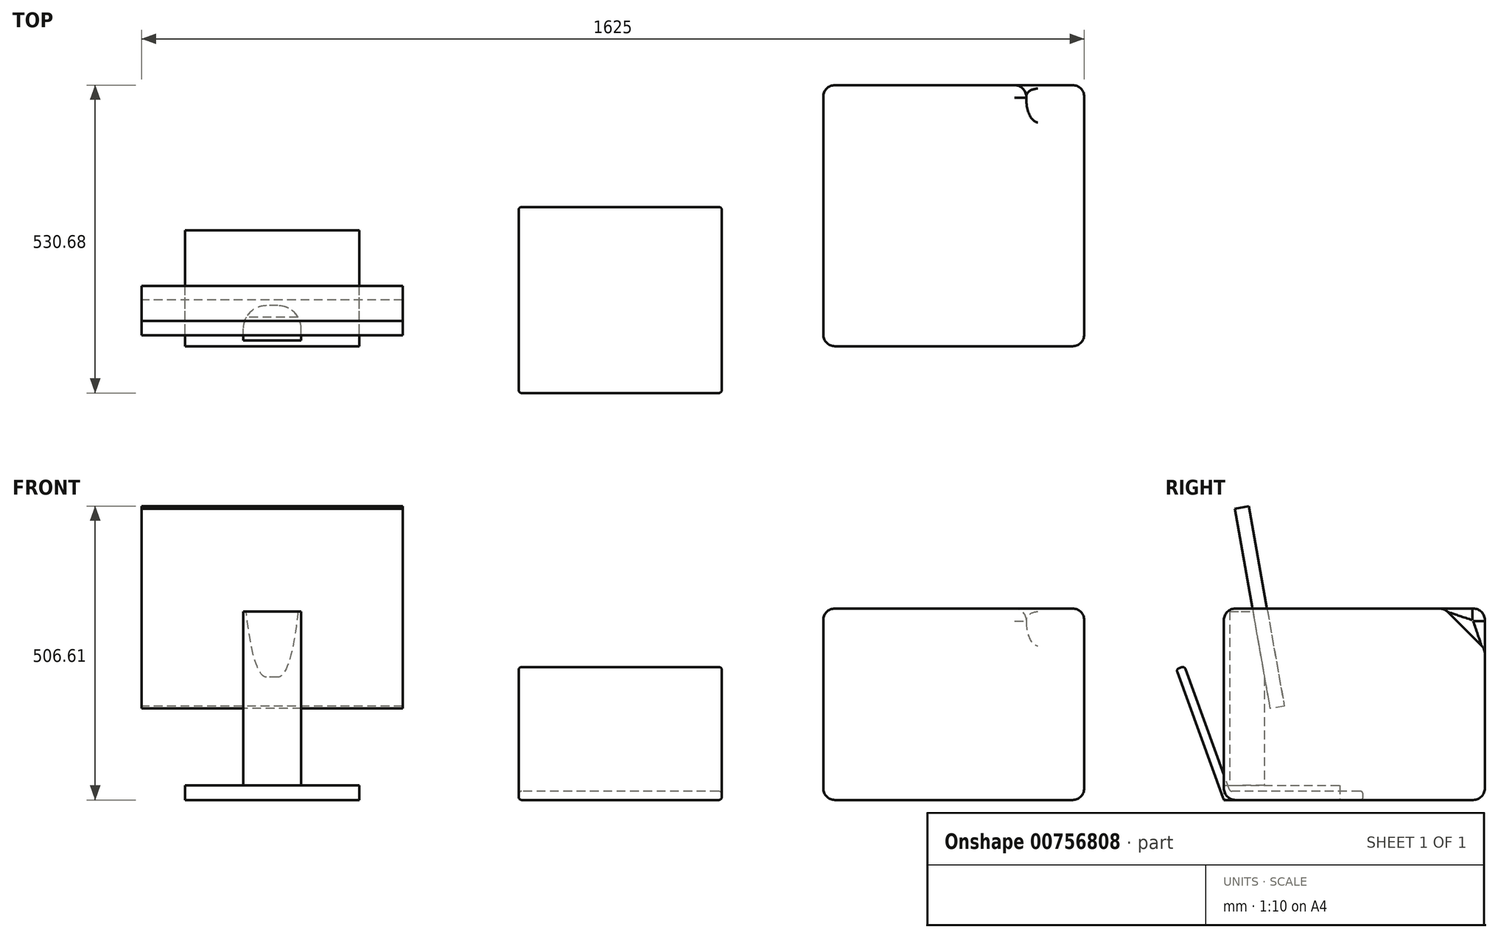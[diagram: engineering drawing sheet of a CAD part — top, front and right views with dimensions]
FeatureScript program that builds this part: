
annotation { "Feature Type Name" : "Feature", "Feature Type Description" : "" }
export const myFeature = defineFeature(function(context is Context, id is Id, definition is map)
    precondition{}
    {
        {
            var Q0;
            Q0=qCreatedBy(makeId("Right.planeOp"),FACE);
            var sketch = newSketch(context, id + "F0", { "sketchPlane" : qUnion([Q0])});
            skLineSegment(sketch, "E0", {"start": v(0, 0) * mm, "end": v(240, 0) * mm});
            skLineSegment(sketch, "E1", {"start": v(240, 0) * mm, "end": v(240, 15) * mm});
            skLineSegment(sketch, "E2", {"start": v(240, 15) * mm, "end": v(10.5, 15) * mm});
            skLineSegment(sketch, "E3", {"start": v(10.5, 15) * mm, "end": v(-67.99, 230.66) * mm});
            skLineSegment(sketch, "E4", {"start": v(-67.99, 230.66) * mm, "end": v(-82.08, 225.53) * mm});
            skLineSegment(sketch, "E5", {"start": v(-82.08, 225.53) * mm, "end": v(0, 0) * mm});
            skSolve(sketch);
        }
        {
            var Q0;
            Q0 = qSketchRegion(id + "F0", true);
            extrude(context, id + "F1", {"entities" : qUnion([Q0]), "endBound" : BoundingType.SYMMETRIC, "depth" : 350 * mm, "offsetDistance" : 25 * mm});
        }
        {
            var Q0;
            Q0=makeQuery(id+"F1.opExtrude","CAP_FACE",FACE,{"disambiguationData":[OSD([sQuery(id+"F0.wireOp",EDGE,"E0"),sQuery(id+"F0.wireOp",EDGE,"E1"),sQuery(id+"F0.wireOp",EDGE,"E2"),sQuery(id+"F0.wireOp",EDGE,"E3"),sQuery(id+"F0.wireOp",EDGE,"E4"),sQuery(id+"F0.wireOp",EDGE,"E5")])],"isStart":false});
            var Q1;
            Q1=makeQuery(id+"F1.opExtrude","SWEPT_EDGE",EDGE,{"disambiguationData":[OSD([sQuery(id+"F0.wireOp",EDGE,"E0"),sQuery(id+"F0.wireOp",EDGE,"E1")])]});
            var Q2;
            Q2=makeQuery(id+"F1.opExtrude","CAP_FACE",FACE,{"disambiguationData":[OSD([sQuery(id+"F0.wireOp",EDGE,"E0"),sQuery(id+"F0.wireOp",EDGE,"E1"),sQuery(id+"F0.wireOp",EDGE,"E2"),sQuery(id+"F0.wireOp",EDGE,"E3"),sQuery(id+"F0.wireOp",EDGE,"E4"),sQuery(id+"F0.wireOp",EDGE,"E5")])],"isStart":true});
            var Q3;
            Q3=makeQuery(id+"F1.opExtrude","SWEPT_EDGE",EDGE,{"disambiguationData":[OSD([sQuery(id+"F0.wireOp",EDGE,"E2"),sQuery(id+"F0.wireOp",EDGE,"E3")])]});
            var Q4;
            Q4=makeQuery(id+"F1.opExtrude","SWEPT_EDGE",EDGE,{"disambiguationData":[OSD([sQuery(id+"F0.wireOp",EDGE,"E1"),sQuery(id+"F0.wireOp",EDGE,"E2")])]});
            var Q5;
            Q5=makeQuery(id+"F1.opExtrude","SWEPT_FACE",FACE,{"disambiguationData":[OSD([sQuery(id+"F0.wireOp",EDGE,"E0")])]});
            var Q6;
            Q6=makeQuery(id+"F1.opExtrude","SWEPT_FACE",FACE,{"disambiguationData":[OSD([sQuery(id+"F0.wireOp",EDGE,"E2")])]});
            var Q7;
            Q7=makeQuery(id+"F1.opExtrude","SWEPT_FACE",FACE,{"disambiguationData":[OSD([sQuery(id+"F0.wireOp",EDGE,"E1")])]});
            var Q8;
            Q8=makeQuery(id+"F1.opExtrude","SWEPT_EDGE",EDGE,{"disambiguationData":[OSD([sQuery(id+"F0.wireOp",EDGE,"E3"),sQuery(id+"F0.wireOp",EDGE,"E4")])]});
            var Q9;
            Q9=makeQuery(id+"F1.opExtrude","SWEPT_EDGE",EDGE,{"disambiguationData":[OSD([sQuery(id+"F0.wireOp",EDGE,"E4"),sQuery(id+"F0.wireOp",EDGE,"E5")])]});
            var Q10;
            Q10=makeQuery(id+"F1.opExtrude","SWEPT_FACE",FACE,{"disambiguationData":[OSD([sQuery(id+"F0.wireOp",EDGE,"E3")])]});
            var Q11;
            Q11=makeQuery(id+"F1.opExtrude","SWEPT_FACE",FACE,{"disambiguationData":[OSD([sQuery(id+"F0.wireOp",EDGE,"E4")])]});
            var Q12;
            Q12=makeQuery(id+"F1.opExtrude","CAP_EDGE",EDGE,{"disambiguationData":[OSD([sQuery(id+"F0.wireOp",EDGE,"E0")])],"isStart":false});
            var Q13;
            Q13=makeQuery(id+"F1.opExtrude","SWEPT_FACE",FACE,{"disambiguationData":[OSD([sQuery(id+"F0.wireOp",EDGE,"E5")])]});
            var Q14;
            Q14=makeQuery(id+"F1.opExtrude","CAP_EDGE",EDGE,{"disambiguationData":[OSD([sQuery(id+"F0.wireOp",EDGE,"E2")])],"isStart":true});
            var Q15;
            Q15=makeQuery(id+"F1.opExtrude","CAP_EDGE",EDGE,{"disambiguationData":[OSD([sQuery(id+"F0.wireOp",EDGE,"E2")])],"isStart":false});
            var Q16;
            Q16=makeQuery(id+"F1.opExtrude","SWEPT_EDGE",EDGE,{"disambiguationData":[OSD([sQuery(id+"F0.wireOp",EDGE,"E0"),sQuery(id+"F0.wireOp",EDGE,"E5")])]});
            var Q17;
            Q17=makeQuery(id+"F1.opExtrude","CAP_EDGE",EDGE,{"disambiguationData":[OSD([sQuery(id+"F0.wireOp",EDGE,"E4")])],"isStart":false});
            var Q18;
            Q18=makeQuery(id+"F1.opExtrude","CAP_EDGE",EDGE,{"disambiguationData":[OSD([sQuery(id+"F0.wireOp",EDGE,"E4")])],"isStart":true});
            var Q19;
            Q19=makeQuery(id+"F1.opExtrude","CAP_EDGE",EDGE,{"disambiguationData":[OSD([sQuery(id+"F0.wireOp",EDGE,"E3")])],"isStart":false});
            var Q20;
            Q20=makeQuery(id+"F1.opExtrude","CAP_EDGE",EDGE,{"disambiguationData":[OSD([sQuery(id+"F0.wireOp",EDGE,"E0")])],"isStart":true});
            var Q21;
            Q21=makeQuery(id+"F1.opExtrude","CAP_EDGE",EDGE,{"disambiguationData":[OSD([sQuery(id+"F0.wireOp",EDGE,"E1")])],"isStart":true});
            var Q22;
            Q22=makeQuery(id+"F1.opExtrude","CAP_EDGE",EDGE,{"disambiguationData":[OSD([sQuery(id+"F0.wireOp",EDGE,"E1")])],"isStart":false});
            var Q23;
            Q23=makeQuery(id+"F1.opExtrude","CAP_EDGE",EDGE,{"disambiguationData":[OSD([sQuery(id+"F0.wireOp",EDGE,"E3")])],"isStart":true});
            var Q24;
            Q24=makeQuery(id+"F1.opExtrude","CAP_EDGE",EDGE,{"disambiguationData":[OSD([sQuery(id+"F0.wireOp",EDGE,"E5")])],"isStart":true});
            var Q25;
            Q25=makeQuery(id+"F1.opExtrude","CAP_EDGE",EDGE,{"disambiguationData":[OSD([sQuery(id+"F0.wireOp",EDGE,"E5")])],"isStart":false});
            fillet(context, id + "F2", {"entities" : qUnion([Q0, Q1, Q2, Q3, Q4, Q5, Q6, Q7, Q8, Q9, Q10, Q11, Q12, Q13, Q14, Q15, Q16, Q17, Q18, Q19, Q20, Q21, Q22, Q23, Q24, Q25]), "radius" : 5 * mm, "tangentPropagation" : true, "allowEdgeOverflow" : false});
        }
        {
            var Q0;
            Q0=qCreatedBy(makeId("Top.planeOp"),FACE);
            var sketch = newSketch(context, id + "F3", { "sketchPlane" : qUnion([Q0])});
            skLineSegment(sketch, "E6.bottom", {"start": v(350, 0) * mm, "end": v(800, 0) * mm});
            skLineSegment(sketch, "E6.top", {"start": v(350, 450) * mm, "end": v(800, 450) * mm});
            skLineSegment(sketch, "E6.left", {"start": v(350, 0) * mm, "end": v(350, 450) * mm});
            skLineSegment(sketch, "E6.right", {"start": v(800, 0) * mm, "end": v(800, 450) * mm});
            skSolve(sketch);
        }
        {
            var Q0;
            Q0 = qSketchRegion(id + "F3", true);
            extrude(context, id + "F4", {"entities" : qUnion([Q0]), "depth" : 330 * mm, "offsetDistance" : 25 * mm});
        }
        {
            var Q0;
            Q0=makeQuery(id+"F4.opExtrude","SWEPT_FACE",FACE,{"disambiguationData":[OSD([sQuery(id+"F3.wireOp",EDGE,"E6.right")])]});
            var sketch = newSketch(context, id + "F5", { "sketchPlane" : qUnion([Q0])});
            skLineSegment(sketch, "E7", {"start": v(380, 330) * mm, "end": v(450, 260) * mm});
            skLineSegment(sketch, "E8", {"start": v(450, 260) * mm, "end": v(450, 330) * mm});
            skLineSegment(sketch, "E9", {"start": v(450, 330) * mm, "end": v(380, 330) * mm});
            skSolve(sketch);
        }
        {
            var Q0;
            Q0 = qSketchRegion(id + "F5", true);
            extrude(context, id + "F6", {"entities" : qUnion([Q0]), "operationType" : NewBodyOperationType.REMOVE, "oppositeDirection" : true, "depth" : 100 * mm, "offsetDistance" : 25 * mm});
        }
        {
            var Q0;
            Q0=makeQuery(id+"F6.boolean.opBoolean","COPY",EDGE,{"derivedFrom":makeQuery(id+"F6.opExtrude","SWEPT_EDGE",EDGE,{"disambiguationData":[OSD([sQuery(id+"F3.wireOp",EDGE,"E6.top"),sQuery(id+"F3.wireOp",EDGE,"E6.right"),sQuery(id+"F5.wireOp",EDGE,"E7"),sQuery(id+"F5.wireOp",EDGE,"E8")])]})});
            var Q1;
            Q1=makeQuery(id+"F4.opExtrude","CAP_EDGE",EDGE,{"disambiguationData":[OSD([sQuery(id+"F3.wireOp",EDGE,"E6.left")])],"isStart":true});
            var Q2;
            Q2=makeQuery(id+"F6.boolean.opBoolean","COPY",FACE,{"derivedFrom":makeQuery(id+"F6.opExtrude","CAP_FACE",FACE,{"disambiguationData":[OSD([sQuery(id+"F5.wireOp",EDGE,"E7"),sQuery(id+"F5.wireOp",EDGE,"E8"),sQuery(id+"F5.wireOp",EDGE,"E9")])],"isStart":false})});
            var Q3;
            Q3=makeQuery(id+"F4.opExtrude","SWEPT_FACE",FACE,{"disambiguationData":[OSD([sQuery(id+"F3.wireOp",EDGE,"E6.left")])]});
            var Q4;
            Q4=makeQuery(id+"F6.boolean.opBoolean","COPY",EDGE,{"derivedFrom":makeQuery(id+"F6.opExtrude","SWEPT_EDGE",EDGE,{"disambiguationData":[OSD([sQuery(id+"F3.wireOp",EDGE,"E6.right"),sQuery(id+"F5.wireOp",EDGE,"E7"),sQuery(id+"F5.wireOp",EDGE,"E9")])]})});
            var Q5;
            Q5=makeQuery(id+"F6.boolean.opBoolean","COPY",FACE,{"derivedFrom":makeQuery(id+"F6.opExtrude","SWEPT_FACE",FACE,{"disambiguationData":[OSD([sQuery(id+"F5.wireOp",EDGE,"E7")])]})});
            var Q6;
            Q6=makeQuery(id+"F4.opExtrude","SWEPT_EDGE",EDGE,{"disambiguationData":[OSD([sQuery(id+"F3.wireOp",EDGE,"E6.top"),sQuery(id+"F3.wireOp",EDGE,"E6.left")])]});
            var Q7;
            Q7=makeQuery(id+"F4.opExtrude","CAP_FACE",FACE,{"disambiguationData":[OSD([sQuery(id+"F3.wireOp",EDGE,"E6.bottom"),sQuery(id+"F3.wireOp",EDGE,"E6.top"),sQuery(id+"F3.wireOp",EDGE,"E6.left"),sQuery(id+"F3.wireOp",EDGE,"E6.right")])],"isStart":true});
            var Q8;
            Q8=makeQuery(id+"F4.opExtrude","SWEPT_FACE",FACE,{"disambiguationData":[OSD([sQuery(id+"F3.wireOp",EDGE,"E6.bottom")])]});
            var Q9;
            Q9=makeQuery(id+"F4.opExtrude","SWEPT_EDGE",EDGE,{"disambiguationData":[OSD([sQuery(id+"F3.wireOp",EDGE,"E6.bottom"),sQuery(id+"F3.wireOp",EDGE,"E6.left")])]});
            var Q10;
            Q10=makeQuery(id+"F4.opExtrude","CAP_FACE",FACE,{"disambiguationData":[OSD([sQuery(id+"F3.wireOp",EDGE,"E6.bottom"),sQuery(id+"F3.wireOp",EDGE,"E6.top"),sQuery(id+"F3.wireOp",EDGE,"E6.left"),sQuery(id+"F3.wireOp",EDGE,"E6.right")])],"isStart":false});
            var Q11;
            Q11=makeQuery(id+"F4.opExtrude","SWEPT_FACE",FACE,{"disambiguationData":[OSD([sQuery(id+"F3.wireOp",EDGE,"E6.top")])]});
            var Q12;
            Q12=makeQuery(id+"F4.opExtrude","SWEPT_FACE",FACE,{"disambiguationData":[OSD([sQuery(id+"F3.wireOp",EDGE,"E6.right")])]});
            var Q13;
            Q13=makeQuery(id+"F6.boolean.opBoolean","COPY",EDGE,{"derivedFrom":makeQuery(id+"F6.opExtrude","CAP_EDGE",EDGE,{"disambiguationData":[OSD([sQuery(id+"F5.wireOp",EDGE,"E9")])],"isStart":false})});
            var Q14;
            Q14=makeQuery(id+"F4.opExtrude","CAP_EDGE",EDGE,{"disambiguationData":[OSD([sQuery(id+"F3.wireOp",EDGE,"E6.right")])],"isStart":true});
            var Q15;
            Q15=makeQuery(id+"F4.opExtrude","CAP_EDGE",EDGE,{"disambiguationData":[OSD([sQuery(id+"F3.wireOp",EDGE,"E6.left")])],"isStart":false});
            var Q16;
            Q16=makeQuery(id+"F4.opExtrude","CAP_EDGE",EDGE,{"disambiguationData":[OSD([sQuery(id+"F3.wireOp",EDGE,"E6.top")])],"isStart":true});
            var Q17;
            Q17=makeQuery(id+"F4.opExtrude","CAP_EDGE",EDGE,{"disambiguationData":[OSD([sQuery(id+"F3.wireOp",EDGE,"E6.bottom")])],"isStart":false});
            var Q18;
            Q18=makeQuery(id+"F4.opExtrude","CAP_EDGE",EDGE,{"disambiguationData":[OSD([sQuery(id+"F3.wireOp",EDGE,"E6.bottom")])],"isStart":true});
            var Q19;
            Q19=makeQuery(id+"F4.opExtrude","SWEPT_EDGE",EDGE,{"disambiguationData":[OSD([sQuery(id+"F3.wireOp",EDGE,"E6.bottom"),sQuery(id+"F3.wireOp",EDGE,"E6.right")])]});
            var Q20;
            Q20=makeQuery(id+"F6.boolean.opBoolean","COPY",EDGE,{"derivedFrom":makeQuery(id+"F6.opExtrude","CAP_EDGE",EDGE,{"disambiguationData":[OSD([sQuery(id+"F5.wireOp",EDGE,"E7")])],"isStart":true})});
            var Q21;
            Q21=makeQuery(id+"F6.boolean.opBoolean","COPY",EDGE,{"derivedFrom":makeQuery(id+"F6.opExtrude","CAP_EDGE",EDGE,{"disambiguationData":[OSD([sQuery(id+"F5.wireOp",EDGE,"E7")])],"isStart":false})});
            var Q22;
            Q22=makeQuery(id+"F6.boolean.opBoolean","COPY",EDGE,{"derivedFrom":makeQuery(id+"F6.opExtrude","CAP_EDGE",EDGE,{"disambiguationData":[OSD([sQuery(id+"F5.wireOp",EDGE,"E8")])],"isStart":false})});
            var Q23;
            Q23=makeQuery(id+"F4.opExtrude","SWEPT_EDGE",EDGE,{"disambiguationData":[OSD([sQuery(id+"F3.wireOp",EDGE,"E6.top"),sQuery(id+"F3.wireOp",EDGE,"E6.right")])]});
            var Q24;
            Q24=makeQuery(id+"F4.opExtrude","CAP_EDGE",EDGE,{"disambiguationData":[OSD([sQuery(id+"F3.wireOp",EDGE,"E6.top")])],"isStart":false});
            var Q25;
            Q25=makeQuery(id+"F4.opExtrude","CAP_EDGE",EDGE,{"disambiguationData":[OSD([sQuery(id+"F3.wireOp",EDGE,"E6.right")])],"isStart":false});
            fillet(context, id + "F7", {"entities" : qUnion([Q0, Q1, Q2, Q3, Q4, Q5, Q6, Q7, Q8, Q9, Q10, Q11, Q12, Q13, Q14, Q15, Q16, Q17, Q18, Q19, Q20, Q21, Q22, Q23, Q24, Q25]), "radius" : 20 * mm, "tangentPropagation" : true, "allowEdgeOverflow" : false});
        }
        {
            var Q0;
            Q0=qCreatedBy(makeId("Top.planeOp"),FACE);
            var sketch = newSketch(context, id + "F8", { "sketchPlane" : qUnion([Q0])});
            skLineSegment(sketch, "E10.bottom", {"start": v(-450, 0) * mm, "end": v(-750, 0) * mm});
            skLineSegment(sketch, "E10.top", {"start": v(-450, 200) * mm, "end": v(-750, 200) * mm});
            skLineSegment(sketch, "E10.left", {"start": v(-450, 0) * mm, "end": v(-450, 200) * mm});
            skLineSegment(sketch, "E10.right", {"start": v(-750, 0) * mm, "end": v(-750, 200) * mm});
            skSolve(sketch);
        }
        {
            var Q0;
            Q0 = qSketchRegion(id + "F8", true);
            extrude(context, id + "F9", {"entities" : qUnion([Q0]), "depth" : 25 * mm, "offsetDistance" : 25 * mm});
        }
        {
            var Q0;
            Q0=makeQuery(id+"F9.opExtrude","CAP_FACE",FACE,{"disambiguationData":[OSD([sQuery(id+"F8.wireOp",EDGE,"E10.bottom"),sQuery(id+"F8.wireOp",EDGE,"E10.top"),sQuery(id+"F8.wireOp",EDGE,"E10.left"),sQuery(id+"F8.wireOp",EDGE,"E10.right")])],"isStart":false});
            var sketch = newSketch(context, id + "F10", { "sketchPlane" : qUnion([Q0])});
            skLineSegment(sketch, "E11.bottom", {"start": v(-550, 10) * mm, "end": v(-650, 10) * mm});
            skLineSegment(sketch, "E11.top", {"start": v(-550, 70) * mm, "end": v(-650, 70) * mm});
            skLineSegment(sketch, "E11.left", {"start": v(-550, 10) * mm, "end": v(-550, 70) * mm});
            skLineSegment(sketch, "E11.right", {"start": v(-650, 10) * mm, "end": v(-650, 70) * mm});
            skLineSegment(sketch, "E12", {"start": v(-600, 0) * mm, "end": v(-600, 10) * mm, "construction": true});
            skSolve(sketch);
        }
        {
            var Q0;
            Q0 = qSketchRegion(id + "F10", true);
            extrude(context, id + "F11", {"entities" : qUnion([Q0]), "operationType" : NewBodyOperationType.ADD, "depth" : 300 * mm, "offsetDistance" : 25 * mm});
        }
        {
            var Q0;
            Q0=makeQuery(id+"F11.opExtrude","CAP_FACE",FACE,{"disambiguationData":[OSD([sQuery(id+"F10.wireOp",EDGE,"E11.bottom"),sQuery(id+"F10.wireOp",EDGE,"E11.top"),sQuery(id+"F10.wireOp",EDGE,"E11.left"),sQuery(id+"F10.wireOp",EDGE,"E11.right")])],"isStart":false});
            var Q1;
            Q1=makeQuery(id+"F11.opExtrude","CAP_EDGE",EDGE,{"disambiguationData":[OSD([sQuery(id+"F10.wireOp",EDGE,"E11.bottom")])],"isStart":false});
            cPlane(context, id + "F12", {"entities" : qUnion([Q0, Q1]), "cplaneType" : CPlaneType.LINE_ANGLE, "offset" : 25 * mm, "angle" : 80 * degree, "width" : 150 * mm, "height" : 150 * mm});
        }
        {
            var Q0;
            Q0=makeQuery(id+"F11.opExtrude","SWEPT_FACE",FACE,{"disambiguationData":[OSD([sQuery(id+"F10.wireOp",EDGE,"E11.right")])]});
            var sketch = newSketch(context, id + "F13", { "sketchPlane" : qUnion([Q0])});
            skLineSegment(sketch, "E13", {"start": v(-50, 325) * mm, "end": v(-70, 211.57) * mm});
            skLineSegment(sketch, "E14", {"start": v(-70, 211.57) * mm, "end": v(-70, 325) * mm});
            skLineSegment(sketch, "E15", {"start": v(-70, 325) * mm, "end": v(-50, 325) * mm});
            skSolve(sketch);
        }
        {
            var Q0;
            Q0 = qSketchRegion(id + "F13", true);
            var Q1;
            Q1=makeQuery(id+"F11.opExtrude","SWEPT_FACE",FACE,{"disambiguationData":[OSD([sQuery(id+"F10.wireOp",EDGE,"E11.left")])]});
            extrude(context, id + "F14", {"entities" : qUnion([Q0]), "operationType" : NewBodyOperationType.REMOVE, "endBound" : BoundingType.UP_TO_SURFACE, "oppositeDirection" : true, "depth" : 25 * mm, "endBoundEntityFace" : qUnion([Q1]), "offsetDistance" : 25 * mm});
        }
        {
            var Q0;
            Q0=makeQuery(id+"F14.boolean.opBoolean","COPY",FACE,{"derivedFrom":makeQuery(id+"F14.opExtrude","SWEPT_FACE",FACE,{"disambiguationData":[OSD([sQuery(id+"F13.wireOp",EDGE,"E13")])]})});
            var sketch = newSketch(context, id + "F15", { "sketchPlane" : qUnion([Q0])});
            skLineSegment(sketch, "E16.bottom", {"start": v(375, 491.38) * mm, "end": v(825, 491.38) * mm});
            skLineSegment(sketch, "E16.top", {"start": v(375, 141.38) * mm, "end": v(825, 141.38) * mm});
            skLineSegment(sketch, "E16.left", {"start": v(375, 491.38) * mm, "end": v(375, 141.38) * mm});
            skLineSegment(sketch, "E16.right", {"start": v(825, 491.38) * mm, "end": v(825, 141.38) * mm});
            skLineSegment(sketch, "E17", {"start": v(600, 311.38) * mm, "end": v(600, 491.38) * mm, "construction": true});
            skSolve(sketch);
        }
        {
            var Q0;
            Q0 = qSketchRegion(id + "F15", true);
            extrude(context, id + "F16", {"entities" : qUnion([Q0]), "operationType" : NewBodyOperationType.ADD, "depth" : 25 * mm, "offsetDistance" : 25 * mm});
        }
        {
            var Q0;
            Q0=makeQuery(id+"F11.opExtrude","SWEPT_EDGE",EDGE,{"disambiguationData":[OSD([sQuery(id+"F10.wireOp",EDGE,"E11.top"),sQuery(id+"F10.wireOp",EDGE,"E11.right")])]});
            var Q1;
            Q1=makeQuery(id+"F11.opExtrude","SWEPT_EDGE",EDGE,{"disambiguationData":[OSD([sQuery(id+"F10.wireOp",EDGE,"E11.top"),sQuery(id+"F10.wireOp",EDGE,"E11.left")])]});
            fillet(context, id + "F17", {"entities" : qUnion([Q0, Q1]), "radius" : 40 * mm, "tangentPropagation" : true, "allowEdgeOverflow" : false});
        }
    });
